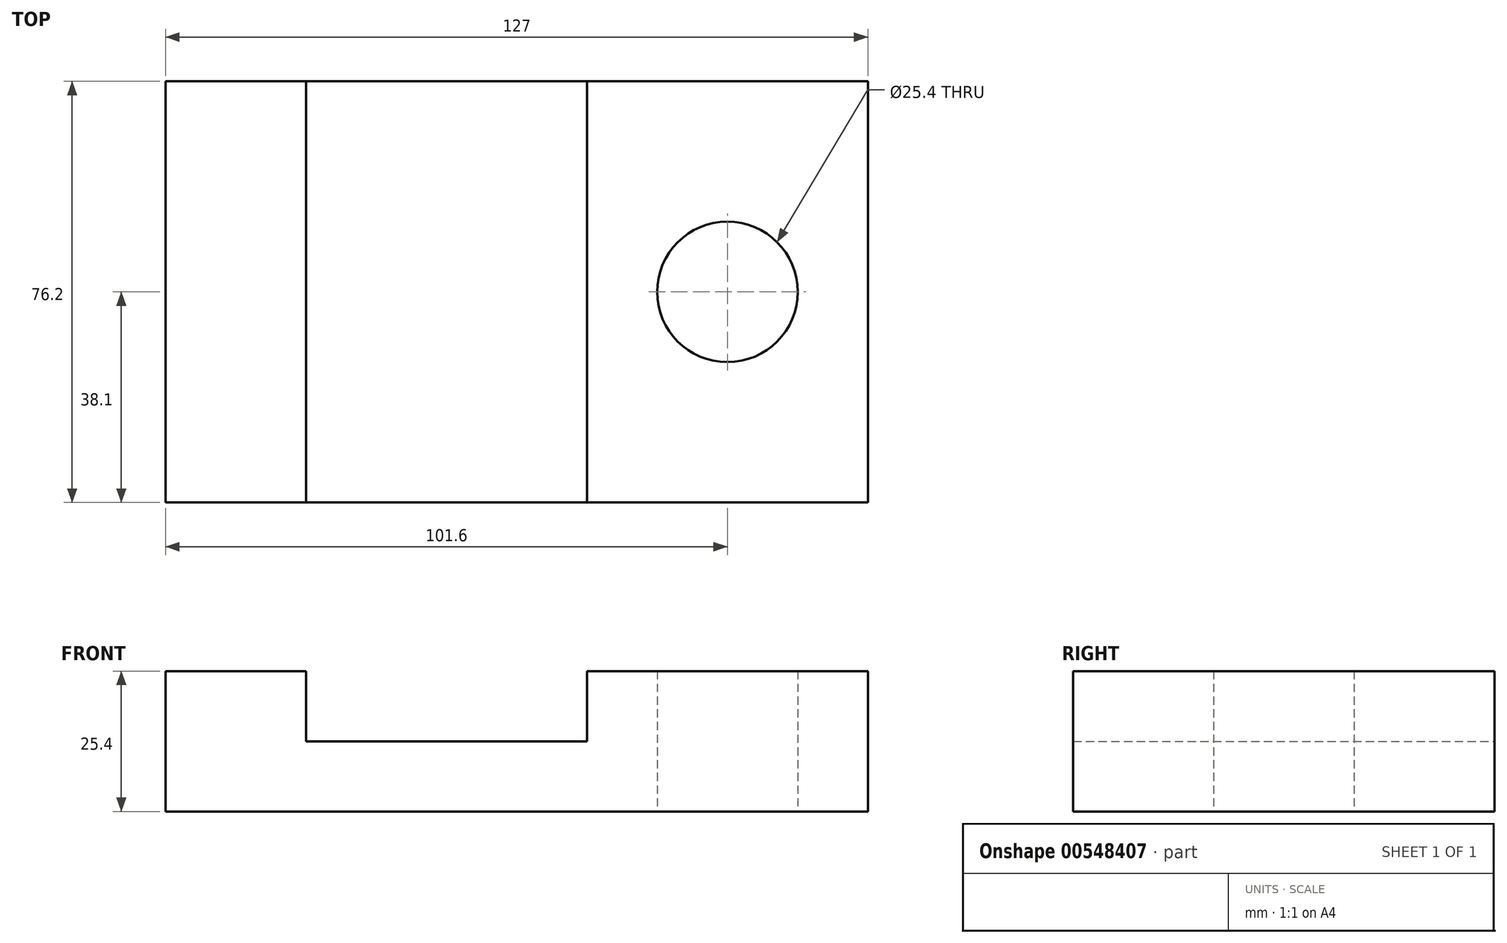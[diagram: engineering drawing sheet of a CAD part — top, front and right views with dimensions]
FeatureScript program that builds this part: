
annotation { "Feature Type Name" : "Feature", "Feature Type Description" : "" }
export const myFeature = defineFeature(function(context is Context, id is Id, definition is map)
    precondition{}
    {
        {
            var Q0;
            Q0=qCreatedBy(makeId("Front.planeOp"),FACE);
            var sketch = newSketch(context, id + "F0", { "sketchPlane" : qUnion([Q0])});
            skLineSegment(sketch, "E0", {"start": v(-60.78, 20.6) * mm, "end": v(-60.78, -4.8) * mm});
            skLineSegment(sketch, "E1", {"start": v(-60.78, -4.8) * mm, "end": v(66.22, -4.8) * mm});
            skLineSegment(sketch, "E2", {"start": v(66.22, -4.8) * mm, "end": v(66.22, 20.6) * mm});
            skLineSegment(sketch, "E3", {"start": v(66.22, 20.6) * mm, "end": v(15.42, 20.6) * mm});
            skLineSegment(sketch, "E4", {"start": v(15.42, 20.6) * mm, "end": v(15.42, 7.9) * mm});
            skLineSegment(sketch, "E5", {"start": v(15.42, 7.9) * mm, "end": v(-35.38, 7.9) * mm});
            skLineSegment(sketch, "E6", {"start": v(-35.38, 7.9) * mm, "end": v(-35.38, 20.6) * mm});
            skLineSegment(sketch, "E7", {"start": v(-35.38, 20.6) * mm, "end": v(-60.78, 20.6) * mm});
            skSolve(sketch);
        }
        {
            var Q0;
            Q0=makeQuery(id+"F0.imprint","IMPRINT",FACE,{"disambiguationData":[TD([[makeQuery(id+"F0.imprint","IMPRINT",EDGE,{"derivedFrom":sQuery(id+"F0.wireOp",EDGE,"E0")}),1.0]])]});
            extrude(context, id + "F1", {"entities" : qUnion([Q0]), "depth" : 76.2 * mm, "offsetDistance" : 25.4 * mm});
        }
        {
            var Q0;
            Q0=qCreatedBy(makeId("Top.planeOp"),FACE);
            var sketch = newSketch(context, id + "F2", { "sketchPlane" : qUnion([Q0])});
            skCircle(sketch, "E8", {"center": v(40.82, -38.1) * mm, "radius": 12.7 * mm});
            skSolve(sketch);
        }
        {
            var Q0;
            Q0 = qSketchRegion(id + "F2", true);
            extrude(context, id + "F3", {"entities" : qUnion([Q0]), "operationType" : NewBodyOperationType.REMOVE, "depth" : 66.8 * mm, "offsetDistance" : 25.4 * mm});
        }
        {
            var Q0;
            Q0 = qSketchRegion(id + "F2", true);
            extrude(context, id + "F4", {"entities" : qUnion([Q0]), "operationType" : NewBodyOperationType.REMOVE, "oppositeDirection" : true, "depth" : 25.4 * mm, "offsetDistance" : 25.4 * mm});
        }
    });
